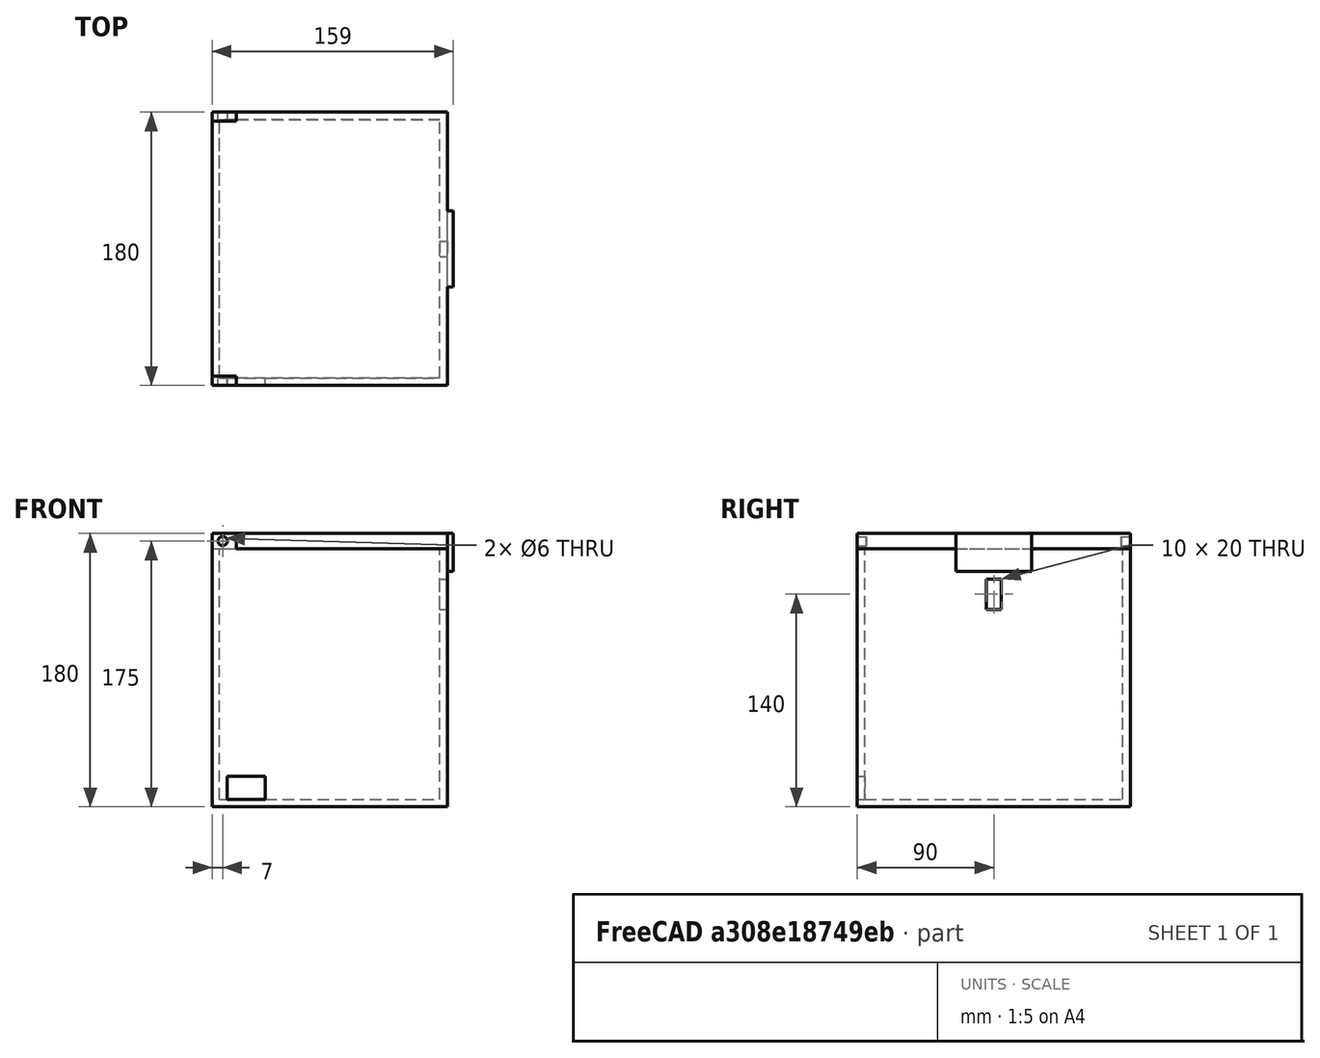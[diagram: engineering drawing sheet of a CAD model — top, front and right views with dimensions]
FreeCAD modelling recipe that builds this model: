
FCSTD DOCUMENT  (FreeCAD 1.0R38806 (Git))
Label: Caja_y tapa
License: All rights reserved
LicenseURL: https://en.wikipedia.org/wiki/All_rights_reserved
objects: Part::Box×14, Part::Cut×11, Part::Fuse×5, Part::Cylinder×4
note: 34 computed .brp shape members not serialized (recipe doc carries the construction recipe); baked Part::Feature solids carry a one-line shape summary decoded from their .brp

FEATURE [Part::Box] Box002  label="tapa"
  AttacherType = Attacher::AttachEngine3D
  Height = 10
  Length = 155
  Placement = pos=(0,0,170) rot=(0,0,1;0rad)
  Width = 180
FEATURE [Part::Box] Box  label="Cube"
  AttacherType = Attacher::AttachEngine3D
  Height = 170
  Length = 155
  Width = 180
FEATURE [Part::Box] Box001  label="Cube001"
  AttacherType = Attacher::AttachEngine3D
  Height = 200
  Length = 145
  Placement = pos=(5,5,5) rot=(0,0,1;0rad)
  Width = 170
FEATURE [Part::Cut] Cut  label="EStructura"
  Base = -> Box
  Refine = true
  Tool = -> Box001
FEATURE [Part::Box] Box003  label="Agujero"
  AttacherType = Attacher::AttachEngine3D
  Height = 15
  Length = 25
  Placement = pos=(10,-7,5) rot=(0,0,1;0rad)
  Width = 25
FEATURE [Part::Cut] Cut001  label="Caja_p1"
  Base = -> Cut
  Refine = true
  Tool = -> Box003
FEATURE [Part::Box] Box004  label="Cube002"
  AttacherType = Attacher::AttachEngine3D
  Height = 25
  Length = 4
  Placement = pos=(155,65,155) rot=(0,0,1;0rad)
  Width = 50
FEATURE [Part::Fuse] Fusion  label="Tapa_1"
  Base = -> Box002
  Refine = true
  Tool = -> Box004
FEATURE [Part::Box] Box005  label="Cube003"
  AttacherType = Attacher::AttachEngine3D
  Height = 20
  Length = 12
  Placement = pos=(146,85,130) rot=(0,0,1;0rad)
  Width = 10
FEATURE [Part::Cut] Cut002  label="Caja"
  Base = -> Cut001
  Refine = true
  Tool = -> Box005
FEATURE [Part::Box] Box006  label="visagra_1_1"
  AttacherType = Attacher::AttachEngine3D
  Height = 10
  Length = 16
  Placement = pos=(0,174,170) rot=(0,0,1;0rad)
  Width = 6
FEATURE [Part::Box] Box007  label="visagra2_1"
  AttacherType = Attacher::AttachEngine3D
  Height = 10
  Length = 16
  Placement = pos=(0,0,170) rot=(0,0,1;0rad)
  Width = 6
FEATURE [Part::Cylinder] Cylinder
  Angle = 360
  AttacherType = Attacher::AttachEngine3D
  FirstAngle = 0
  Height = 148
  Placement = pos=(7,192,175) rot=(1,0,0;1.5708rad)
  Radius = 3
  SecondAngle = 0
FEATURE [Part::Cut] Cut003  label="visagra1"
  Base = -> Box006
  Refine = true
  Tool = -> Cylinder
FEATURE [Part::Cylinder] Cylinder001
  Angle = 360
  AttacherType = Attacher::AttachEngine3D
  FirstAngle = 0
  Height = 148
  Placement = pos=(7,139,175) rot=(1,0,0;1.5708rad)
  Radius = 3
  SecondAngle = 0
FEATURE [Part::Cut] Cut004  label="visagra2"
  Base = -> Box007
  Refine = true
  Tool = -> Cylinder001
FEATURE [Part::Fuse] Fusion001
  Base = -> Cut002
  Refine = true
  Tool = -> Cut003
FEATURE [Part::Fuse] Fusion002
  Base = -> Fusion001
  Refine = true
  Tool = -> Cut004
FEATURE [Part::Cut] Cut005  label="Tapa"
  Base = -> Fusion
  Refine = true
  Tool = -> Fusion002
FEATURE [Part::Box] Box008  label="Cube004"
  AttacherType = Attacher::AttachEngine3D
  Height = 170
  Length = 155
  Width = 180
FEATURE [Part::Box] Box009  label="Cube005"
  AttacherType = Attacher::AttachEngine3D
  Height = 200
  Length = 145
  Placement = pos=(5,5,5) rot=(0,0,1;0rad)
  Width = 170
FEATURE [Part::Box] Box010  label="Agujero001"
  AttacherType = Attacher::AttachEngine3D
  Height = 15
  Length = 25
  Placement = pos=(10,-7,5) rot=(0,0,1;0rad)
  Width = 25
FEATURE [Part::Box] Box011  label="Cube006"
  AttacherType = Attacher::AttachEngine3D
  Height = 20
  Length = 12
  Placement = pos=(146,85,130) rot=(0,0,1;0rad)
  Width = 10
FEATURE [Part::Box] Box012  label="visagra_1_002"
  AttacherType = Attacher::AttachEngine3D
  Height = 10
  Length = 16
  Placement = pos=(0,174,170) rot=(0,0,1;0rad)
  Width = 6
FEATURE [Part::Box] Box013  label="visagra2_002"
  AttacherType = Attacher::AttachEngine3D
  Height = 10
  Length = 16
  Placement = pos=(0,0,170) rot=(0,0,1;0rad)
  Width = 6
FEATURE [Part::Cut] Cut006  label="EStructura001"
  Base = -> Box008
  Refine = true
  Tool = -> Box009
FEATURE [Part::Cut] Cut007  label="Caja_p002"
  Base = -> Cut006
  Refine = true
  Tool = -> Box010
FEATURE [Part::Cut] Cut008  label="Caja001"
  Base = -> Cut007
  Refine = true
  Tool = -> Box011
FEATURE [Part::Cylinder] Cylinder002
  Angle = 360
  AttacherType = Attacher::AttachEngine3D
  FirstAngle = 0
  Height = 148
  Placement = pos=(7,192,175) rot=(1,0,0;1.5708rad)
  Radius = 3
  SecondAngle = 0
FEATURE [Part::Cut] Cut009  label="visagra003"
  Base = -> Box012
  Refine = true
  Tool = -> Cylinder002
FEATURE [Part::Cylinder] Cylinder003
  Angle = 360
  AttacherType = Attacher::AttachEngine3D
  FirstAngle = 0
  Height = 148
  Placement = pos=(7,139,175) rot=(1,0,0;1.5708rad)
  Radius = 3
  SecondAngle = 0
FEATURE [Part::Cut] Cut010  label="visagra004"
  Base = -> Box013
  Refine = true
  Tool = -> Cylinder003
FEATURE [Part::Fuse] Fusion003
  Base = -> Cut008
  Refine = true
  Tool = -> Cut009
FEATURE [Part::Fuse] Fusion004  label="Caja002"
  Base = -> Fusion003
  Refine = true
  Tool = -> Cut010
